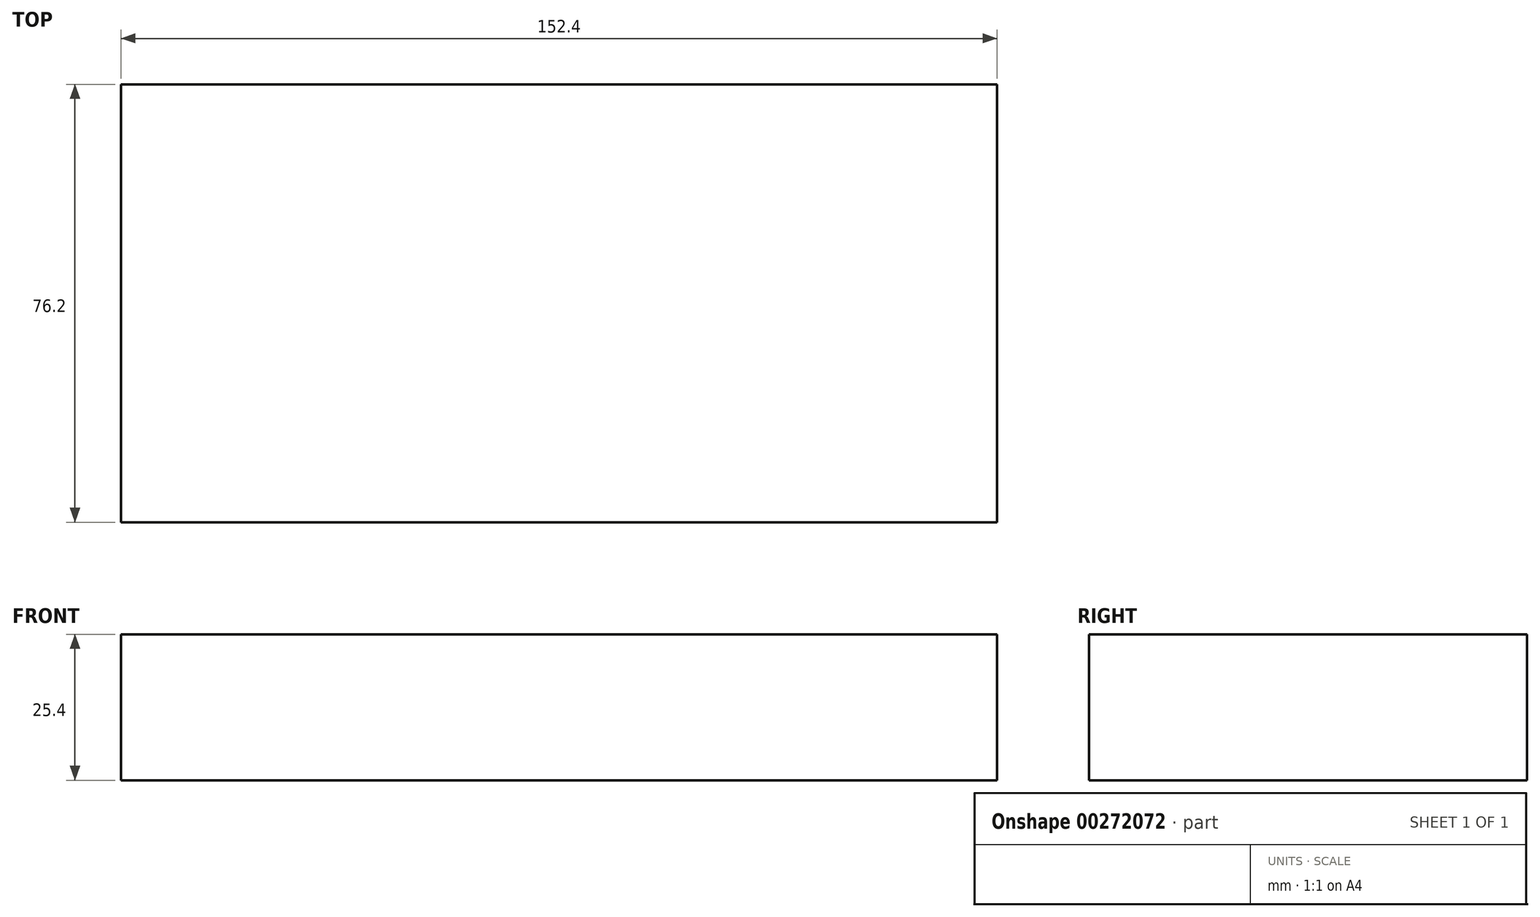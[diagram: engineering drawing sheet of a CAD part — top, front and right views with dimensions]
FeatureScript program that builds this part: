
annotation { "Feature Type Name" : "Feature", "Feature Type Description" : "" }
export const myFeature = defineFeature(function(context is Context, id is Id, definition is map)
    precondition{}
    {
        {
            var Q0;
            Q0=qCreatedBy(makeId("Front.planeOp"),FACE);
            var sketch = newSketch(context, id + "F0", { "sketchPlane" : qUnion([Q0])});
            skLineSegment(sketch, "E0.bottom", {"start": v(0, 6.15) * mm, "end": v(-152.4, 6.15) * mm});
            skLineSegment(sketch, "E0.top", {"start": v(0, 31.55) * mm, "end": v(-152.4, 31.55) * mm});
            skLineSegment(sketch, "E0.left", {"start": v(0, 6.15) * mm, "end": v(0, 31.55) * mm});
            skLineSegment(sketch, "E0.right", {"start": v(-152.4, 6.15) * mm, "end": v(-152.4, 31.55) * mm});
            skPoint(sketch, "E0.middle", {"position": v(-76.2, 18.85) * mm});
            skSolve(sketch);
        }
        {
            var Q0;
            Q0=makeQuery(id+"F0.imprint","IMPRINT",FACE,{"disambiguationData":[TD([[makeQuery(id+"F0.imprint","IMPRINT",EDGE,{"derivedFrom":sQuery(id+"F0.wireOp",EDGE,"E0.bottom")}),-1.0]])]});
            extrude(context, id + "F1", {"entities" : qUnion([Q0]), "depth" : 76.2 * mm});
        }
    });
